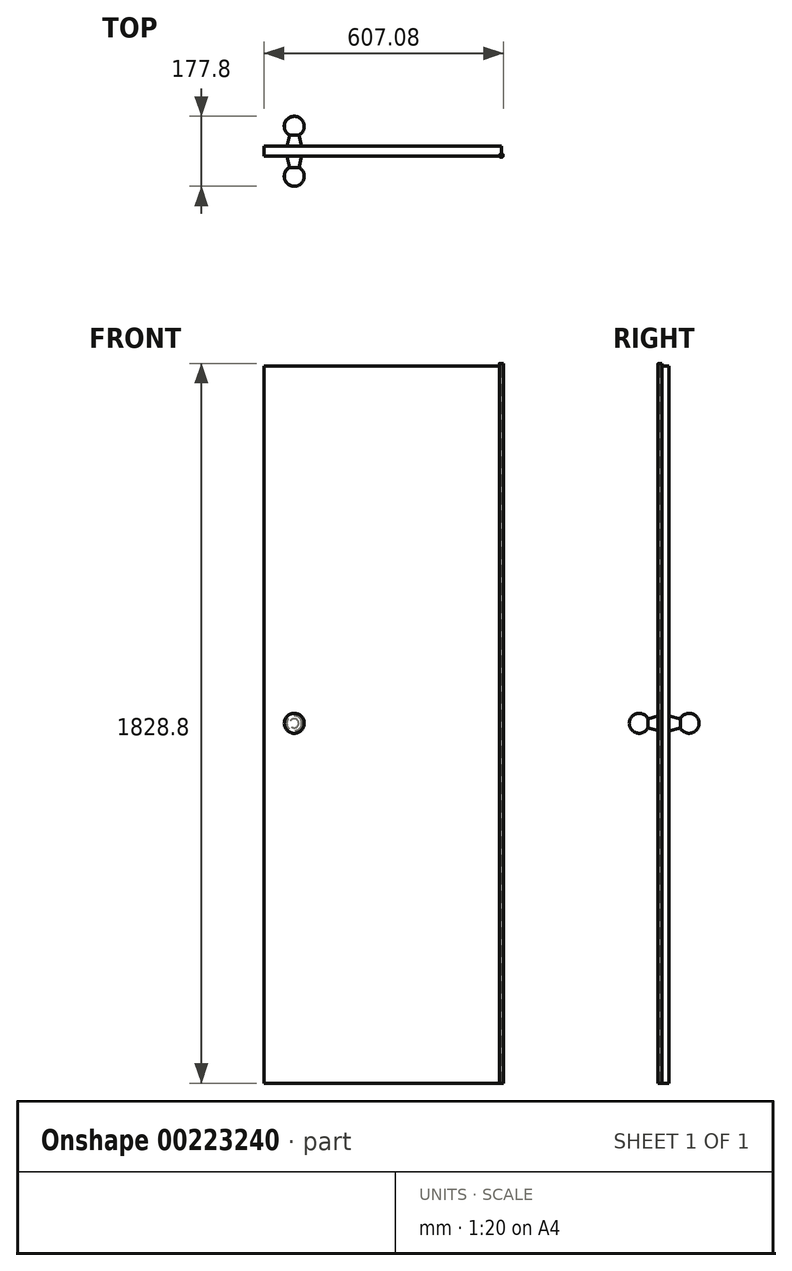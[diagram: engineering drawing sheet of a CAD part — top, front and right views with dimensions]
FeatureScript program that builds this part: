
annotation { "Feature Type Name" : "Feature", "Feature Type Description" : "" }
export const myFeature = defineFeature(function(context is Context, id is Id, definition is map)
    precondition{}
    {
        {
            var Q0;
            Q0=qCreatedBy(makeId("Front.planeOp"),FACE);
            var sketch = newSketch(context, id + "F0", { "sketchPlane" : qUnion([Q0])});
            skLineSegment(sketch, "E0.bottom", {"start": v(0, 0) * mm, "end": v(603.25, 0) * mm});
            skLineSegment(sketch, "E0.top", {"start": v(0, 1822.45) * mm, "end": v(603.25, 1822.45) * mm});
            skLineSegment(sketch, "E0.left", {"start": v(0, 0) * mm, "end": v(0, 1822.45) * mm});
            skLineSegment(sketch, "E0.right", {"start": v(603.25, 0) * mm, "end": v(603.25, 1822.45) * mm});
            skLineSegment(sketch, "E1", {"start": v(-183.2, 914.4) * mm, "end": v(165.94, 914.4) * mm});
            skLineSegment(sketch, "E2", {"start": v(76.2, 1062.27) * mm, "end": v(76.2, 800.41) * mm});
            skCircle(sketch, "E3", {"center": v(76.2, 914.4) * mm, "radius": 73.32 * mm, "construction": true});
            skSolve(sketch);
        }
        {
            var Q0;
            Q0=qSketchRegion(id+"F0",true);
            extrude(context, id + "F1", {"entities" : qUnion([Q0]), "depth" : 25.4 * mm});
        }
        {
            var Q0;
            Q0=qCreatedBy(makeId("Top.planeOp"),FACE);
            cPlane(context, id + "F2", {"entities" : qUnion([Q0]), "cplaneType" : CPlaneType.OFFSET, "offset" : 914.4 * mm, "width" : 152.4 * mm, "height" : 152.4 * mm});
        }
        {
            var Q0;
            Q0=qCreatedBy(id+"F2.planeOp",FACE);
            var sketch = newSketch(context, id + "F3", { "sketchPlane" : qUnion([Q0])});
            skArc(sketch, "E4", {"start": v(64.7, -53.56) * mm, "mid": v(51.5, -82.12) * mm, "end": v(76.2, -101.6) * mm});
            skLineSegment(sketch, "E5", {"start": v(57.15, -25.4) * mm, "end": v(64.7, -53.56) * mm});
            skLineSegment(sketch, "E6", {"start": v(76.2, -25.4) * mm, "end": v(57.15, -25.4) * mm});
            skLineSegment(sketch, "E7", {"start": v(76.2, -25.4) * mm, "end": v(76.2, -101.6) * mm});
            skSolve(sketch);
        }
        {
            var Q0;
            Q0=makeQuery(id+"F1.opExtrude","CAP_FACE",FACE,{"disambiguationData":[OSD([sQuery(id+"F0.wireOp",EDGE,"E0.bottom"),sQuery(id+"F0.wireOp",EDGE,"E0.top"),sQuery(id+"F0.wireOp",EDGE,"E0.left"),sQuery(id+"F0.wireOp",EDGE,"E0.right")])],"isStart":false});
            var sketch = newSketch(context, id + "F4", { "sketchPlane" : qUnion([Q0])});
            skCircle(sketch, "E8", {"center": v(76.2, 914.4) * mm, "radius": 21.63 * mm});
            skSolve(sketch);
        }
        {
            var Q0;
            Q0=makeQuery(id+"F3.imprint","IMPRINT",FACE,{"disambiguationData":[TD([[makeQuery(id+"F3.imprint","IMPRINT",EDGE,{"derivedFrom":sQuery(id+"F3.wireOp",EDGE,"E4")}),1.0]])]});
            var Q1;
            Q1=sQuery(id+"F4.wireOp",EDGE,"E8");
            sweep(context, id + "F5", {"profiles" : qUnion([Q0]), "path" : qUnion([Q1])});
        }
        {
            var Q0;
            Q0=qCreatedBy(makeId("Front.planeOp"),FACE);
            cPlane(context, id + "F6", {"entities" : qUnion([Q0]), "cplaneType" : CPlaneType.OFFSET, "offset" : 12.7 * mm, "width" : 152.4 * mm, "height" : 152.4 * mm});
        }
        {
            var Q0;
            Q0=makeQuery(id+"F5.opSweep","SWEPT_BODY",BODY,{"disambiguationData":[OSD([sQuery(id+"F3.wireOp",EDGE,"E4"),sQuery(id+"F3.wireOp",EDGE,"E5"),sQuery(id+"F3.wireOp",EDGE,"E6"),sQuery(id+"F3.wireOp",EDGE,"E7"),sQuery(id+"F4.wireOp",EDGE,"E8")])]});
            var Q1;
            Q1=qCreatedBy(id+"F6.planeOp",FACE);
            mirror(context, id + "F7", {"operationType" : NewBodyOperationType.ADD, "entities" : qUnion([Q0]), "mirrorPlane" : qUnion([Q1])});
        }
        {
            var Q0;
            Q0=qCreatedBy(makeId("Top.planeOp"),FACE);
            var sketch = newSketch(context, id + "F8", { "sketchPlane" : qUnion([Q0])});
            skCircle(sketch, "E9", {"center": v(602.32, -23.37) * mm, "radius": 4.76 * mm});
            skSolve(sketch);
        }
        {
            var Q0;
            Q0=qSketchRegion(id+"F8",true);
            extrude(context, id + "F9", {"entities" : qUnion([Q0]), "operationType" : NewBodyOperationType.ADD, "depth" : 1828.8 * mm});
        }
    });
